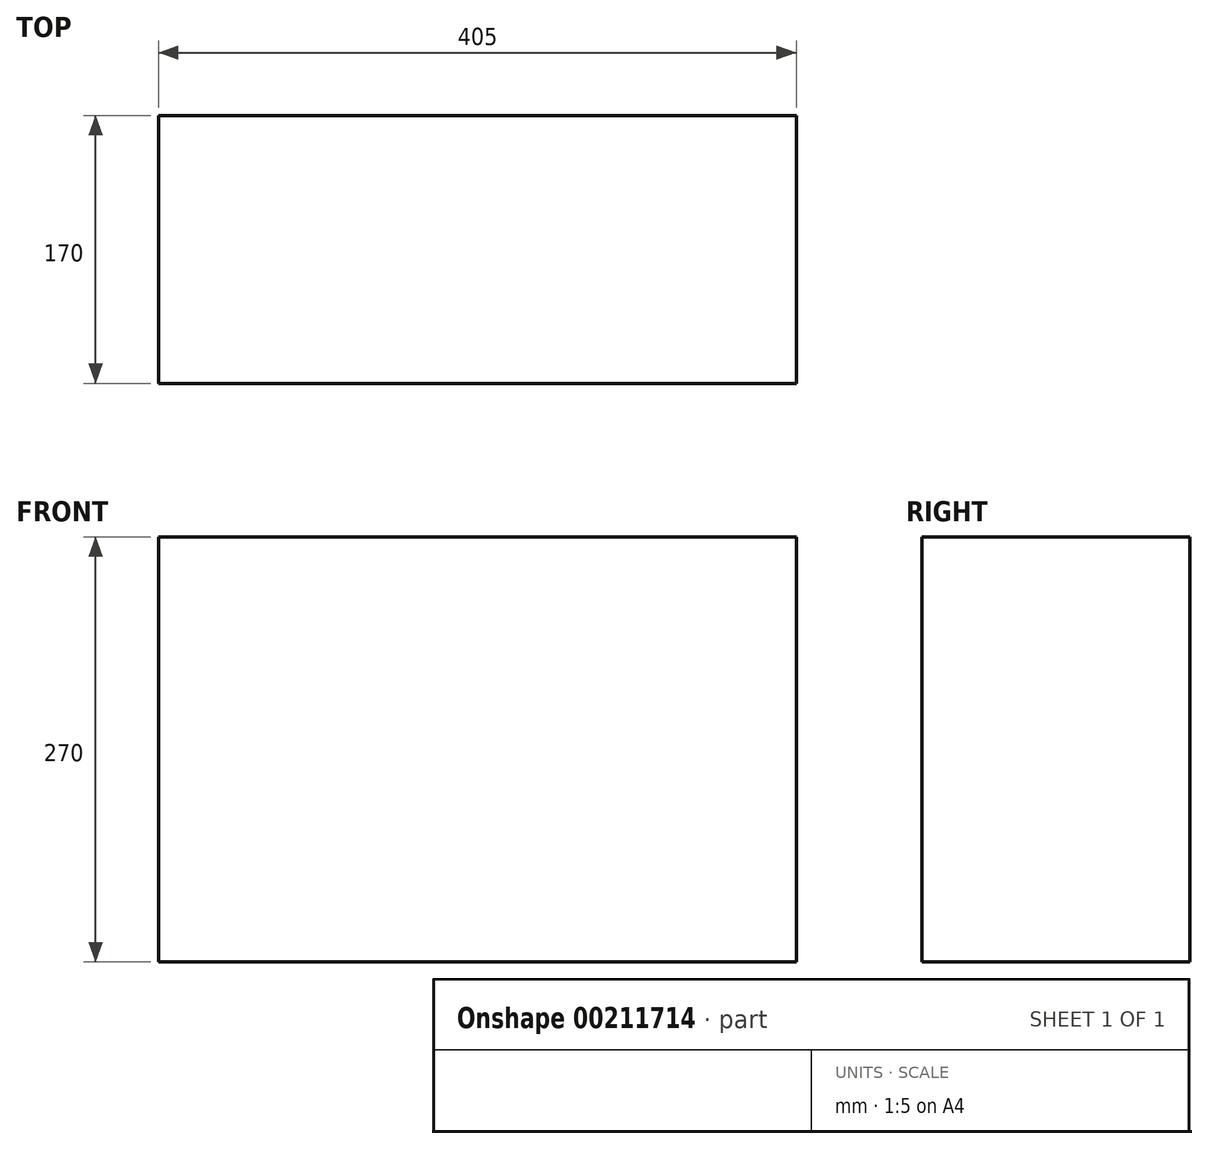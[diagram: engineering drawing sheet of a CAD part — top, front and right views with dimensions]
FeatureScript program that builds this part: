
annotation { "Feature Type Name" : "Feature", "Feature Type Description" : "" }
export const myFeature = defineFeature(function(context is Context, id is Id, definition is map)
    precondition{}
    {
        {
            var Q0;
            Q0=qCreatedBy(makeId("Top.planeOp"),FACE);
            var sketch = newSketch(context, id + "F0", { "sketchPlane" : qUnion([Q0])});
            skLineSegment(sketch, "E0.bottom", {"start": v(202.5, 85) * mm, "end": v(-202.5, 85) * mm});
            skLineSegment(sketch, "E0.top", {"start": v(202.5, -85) * mm, "end": v(-202.5, -85) * mm});
            skLineSegment(sketch, "E0.left", {"start": v(202.5, 85) * mm, "end": v(202.5, -85) * mm});
            skLineSegment(sketch, "E0.right", {"start": v(-202.5, 85) * mm, "end": v(-202.5, -85) * mm});
            skPoint(sketch, "E0.middle", {"position": v(0, 0) * mm});
            skSolve(sketch);
        }
        {
            var Q0;
            Q0=qCreatedBy(makeId("Front.planeOp"),FACE);
            var sketch = newSketch(context, id + "F1", { "sketchPlane" : qUnion([Q0])});
            skLineSegment(sketch, "E1", {"start": v(0, 0) * mm, "end": v(0, 270) * mm});
            skSolve(sketch);
        }
        {
            var Q0;
            Q0=makeQuery(id+"F0.imprint","IMPRINT",FACE,{"disambiguationData":[TD([[makeQuery(id+"F0.imprint","IMPRINT",EDGE,{"derivedFrom":sQuery(id+"F0.wireOp",EDGE,"E0.bottom")}),1.0]])]});
            var Q1;
            Q1=sQuery(id+"F1.wireOp",EDGE,"E1");
            sweep(context, id + "F2", {"profiles" : qUnion([Q0]), "path" : qUnion([Q1])});
        }
    });
